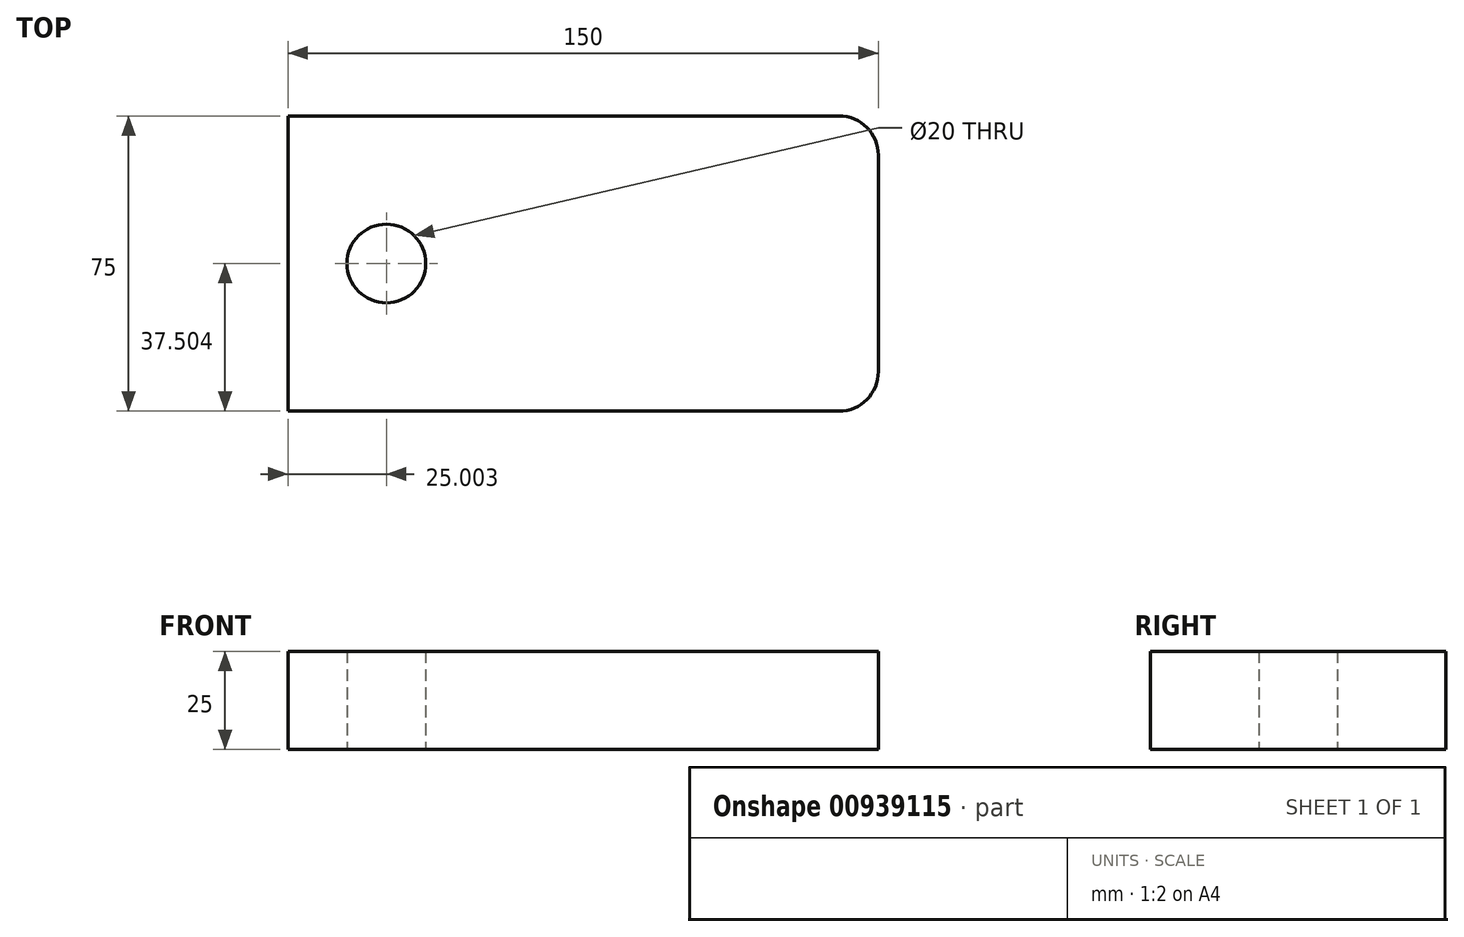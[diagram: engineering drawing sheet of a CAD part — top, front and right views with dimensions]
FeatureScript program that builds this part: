
annotation { "Feature Type Name" : "Feature", "Feature Type Description" : "" }
export const myFeature = defineFeature(function(context is Context, id is Id, definition is map)
    precondition{}
    {
        {
            var Q0;
            Q0=qCreatedBy(makeId("Top.planeOp"),FACE);
            var sketch = newSketch(context, id + "F0", { "sketchPlane" : qUnion([Q0])});
            skLineSegment(sketch, "E0.bottom", {"start": v(-70.56, 45.96) * mm, "end": v(69.44, 45.96) * mm});
            skLineSegment(sketch, "E0.top", {"start": v(-70.56, -29.04) * mm, "end": v(69.44, -29.04) * mm});
            skLineSegment(sketch, "E0.left", {"start": v(-70.56, 45.96) * mm, "end": v(-70.56, -29.04) * mm});
            skLineSegment(sketch, "E0.right", {"start": v(79.44, 35.96) * mm, "end": v(79.44, -19.04) * mm});
            skCircle(sketch, "E1", {"center": v(-45.56, 8.46) * mm, "radius": 10 * mm});
            skPoint(sketch, "E2.visualSharp", {"position": v(79.44, 45.96) * mm});
            skArc(sketch, "E2.filletArc", {"start": v(79.44, 35.96) * mm, "mid": v(76.51, 43.03) * mm, "end": v(69.44, 45.96) * mm});
            skPoint(sketch, "E3.visualSharp", {"position": v(79.44, -29.04) * mm});
            skArc(sketch, "E3.filletArc", {"start": v(69.44, -29.04) * mm, "mid": v(76.51, -26.1) * mm, "end": v(79.44, -19.04) * mm});
            skSolve(sketch);
        }
        {
            var Q0;
            Q0=makeQuery(id+"F0.imprint","IMPRINT",FACE,{"disambiguationData":[TD([[makeQuery(id+"F0.imprint","IMPRINT",EDGE,{"derivedFrom":sQuery(id+"F0.wireOp",EDGE,"E0.bottom")}),-1.0]])]});
            extrude(context, id + "F1", {"entities" : qUnion([Q0]), "depth" : 25 * mm, "offsetDistance" : 25 * mm});
        }
    });
